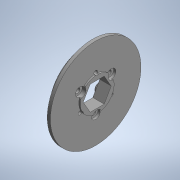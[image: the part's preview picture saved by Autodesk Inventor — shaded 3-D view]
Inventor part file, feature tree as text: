
AUTODESK INVENTOR PART (.ipt)
format: ipt  version: 2020 (Build 240168000, 168)  size: 414,208 bytes
history: native  units: mm (DEFAULTED — no unit token found)
features: chamfer x1
ambient origin geometry x8: Origin, YZ Plane, XZ Plane, XY Plane, X Axis, Y Axis, Z Axis, Center Point
bodies: Solid1 (feature_tree)
feature tree (1):
  chamfer  "Chamfer2"  [1 undecoded]
note: 1 required parameter value undecoded (feature->parameter linkage not recoverable at this tier; creation-order binding heuristic only, values carry confidence <= 0.55)
